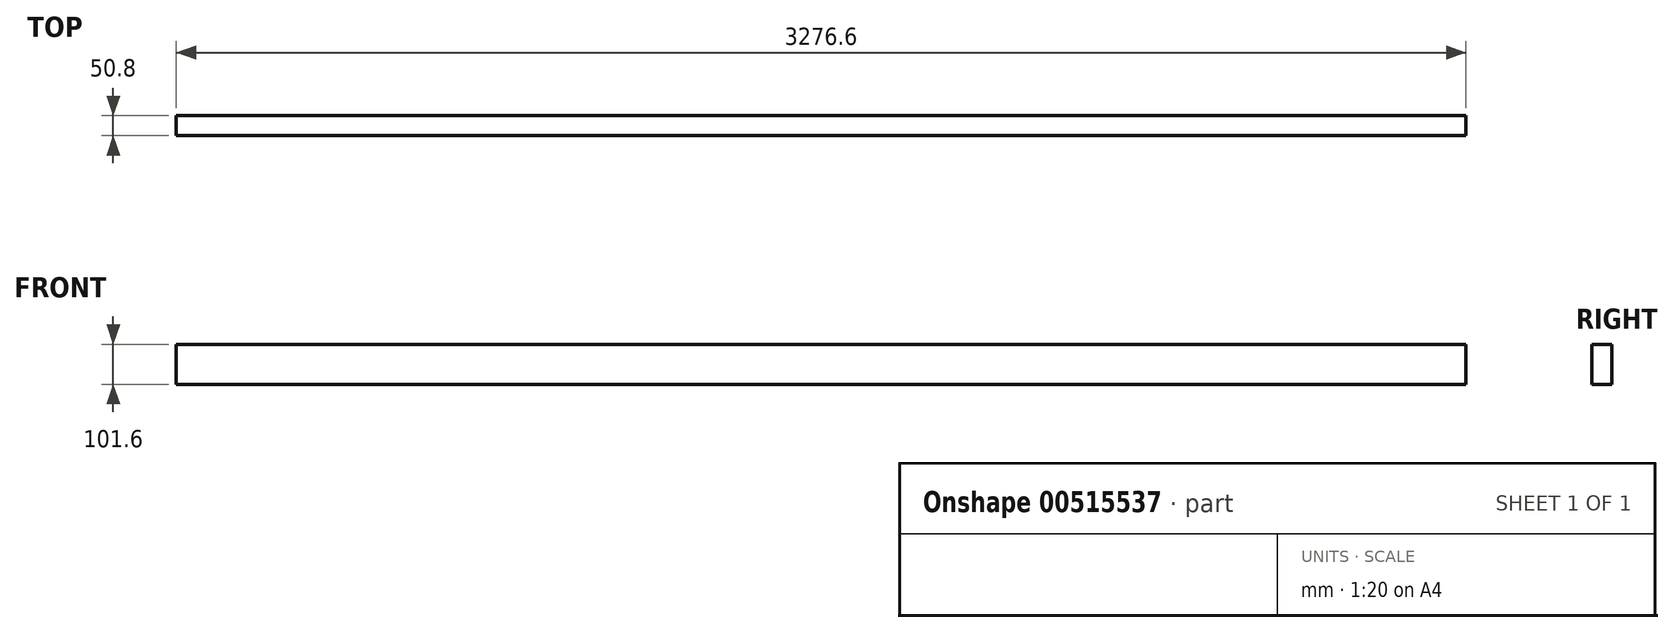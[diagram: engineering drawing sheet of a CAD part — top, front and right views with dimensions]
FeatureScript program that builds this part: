
annotation { "Feature Type Name" : "Feature", "Feature Type Description" : "" }
export const myFeature = defineFeature(function(context is Context, id is Id, definition is map)
    precondition{}
    {
        {
            var Q0;
            Q0=qCreatedBy(makeId("Right.planeOp"),FACE);
            var sketch = newSketch(context, id + "F0", { "sketchPlane" : qUnion([Q0])});
            skLineSegment(sketch, "E0.bottom", {"start": v(0, 0) * mm, "end": v(-50.8, 0) * mm});
            skLineSegment(sketch, "E0.top", {"start": v(0, 101.6) * mm, "end": v(-50.8, 101.6) * mm});
            skLineSegment(sketch, "E0.left", {"start": v(0, 0) * mm, "end": v(0, 101.6) * mm});
            skLineSegment(sketch, "E0.right", {"start": v(-50.8, 0) * mm, "end": v(-50.8, 101.6) * mm});
            skSolve(sketch);
        }
        {
            var Q0;
            Q0=makeQuery(id+"F0.imprint","IMPRINT",FACE,{"disambiguationData":[TD([[makeQuery(id+"F0.imprint","IMPRINT",EDGE,{"derivedFrom":sQuery(id+"F0.wireOp",EDGE,"E0.bottom")}),-1.0]])]});
            extrude(context, id + "F1", {"entities" : qUnion([Q0]), "oppositeDirection" : true, "depth" : 3276.6 * mm, "offsetDistance" : 25.4 * mm});
        }
    });
